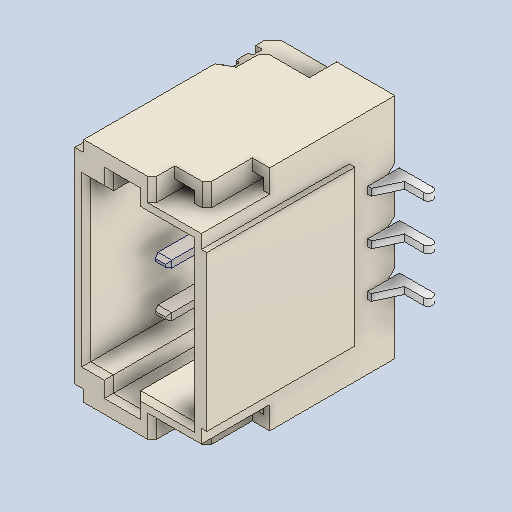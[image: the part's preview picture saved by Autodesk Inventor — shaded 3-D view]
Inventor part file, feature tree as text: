
AUTODESK INVENTOR PART (.ipt)
format: ipt  version: 2024.3 (Build 283343000, 343)  size: 266,752 bytes
history: native  units: in
note: dims shown in document units (in); Inventor stores cm internally (conversion verified against a paired STEP export)
features: other x4, chamfer x1, mirror x1
ambient origin geometry x8: Origin, YZ Plane, XZ Plane, XY Plane, X Axis, Y Axis, Z Axis, Center Point
bodies: Solid1 (feature_tree), Solid2 (feature_tree), Solid3 (feature_tree), Solid4 (feature_tree), Solid5 (feature_tree), Solid6 (feature_tree), Solid7 (feature_tree), Solid8 (feature_tree), Solid9 (feature_tree)
feature tree (6):
  other  "Boss-Extrude2"
  chamfer  "Chamfer3"  [1 undecoded]
  mirror  "Mirror2"
  other  "Szyk liniowy1"
  other  "Szyk liniowy3[1]"
  other  "Szyk liniowy3[2]"
note: 1 required parameter value undecoded (feature->parameter linkage not recoverable at this tier; creation-order binding heuristic only, values carry confidence <= 0.55)
